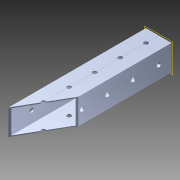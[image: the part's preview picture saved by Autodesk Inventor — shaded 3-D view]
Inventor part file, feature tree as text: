
AUTODESK INVENTOR PART (.ipt)
format: ipt  version: 2014 SP1 (Build 180222100, 222)  size: 1,264,128 bytes
history: native  units: in
note: dims shown in document units (in); Inventor stores cm internally (conversion verified against a paired STEP export)
features: extrude x2, sketch x2, pattern_circular x1, other x1, plane x1, imported_body x1
ambient origin geometry x8: Origin, YZ Plane, XZ Plane, XY Plane, X Axis, Y Axis, Z Axis, Center Point
bodies: Body1 (feature_tree)
feature tree (8):
  pattern_circular  "CirPattern2"
  other  "217-3426-STEP1"
  plane  "Work Plane1"
  extrude  "Extrusion1"  Depth=3937.0079in TaperAngle=0.0deg
  extrude  "Extrusion3"  [1 undecoded]
  imported_body  "Base1"
  sketch  "Sketch1"  dims[d0=-21.0in d1=3937.0079in d2=0.0in]
  sketch  "Sketch4"  dims[d5=3.937in d6=0.0in]
note: 1 required parameter value undecoded (feature->parameter linkage not recoverable at this tier; creation-order binding heuristic only, values carry confidence <= 0.55)
